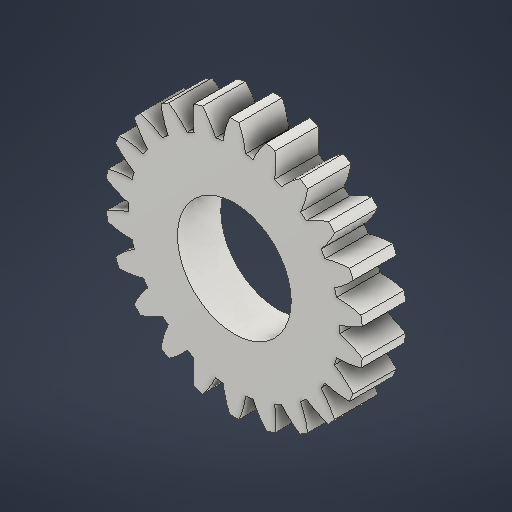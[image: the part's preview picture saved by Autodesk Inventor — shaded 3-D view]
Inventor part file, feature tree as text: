
AUTODESK INVENTOR PART (.ipt)
format: ipt  version: 2025.3 (Build 293356030, 356C)  size: 342,016 bytes
history: native  units: mm (DEFAULTED — no unit token found)
features: plane x3, other x3, extrude x2, sketch x2
ambient origin geometry x8: Origin, YZ Plane, XZ Plane, XY Plane, X Axis, Y Axis, Z Axis, Center Point
bodies: Solid1 (feature_tree)
feature tree (10):
  extrude  "Extrusion1"  Depth=4.0mm TaperAngle=0.0deg
  plane  "Work Plane2"
  plane  "Work Plane8"
  plane  "Work Plane9"
  other  "Spur Gear"
  extrude  "Extrusion2"  Depth=10.0mm TaperAngle=0.0deg
  sketch  "Sketch1"  dims[d0=23.748125mm d1=4.0mm d2=0.0mm]
  other  "Srf1"
  sketch  "Sketch3"  dims[d3=20.9mm d4=10.0mm d5=0.0mm d16=40.0mm d17=0.0mm d34=1.427997mm d39=0.0mm d41=0.0mm d43=40.0mm d46=40.0mm d47=0.0mm d48=0.0mm d49=10.5mm d50=10.0mm d51=0.0mm]
  other  "Pitch Diameter"
